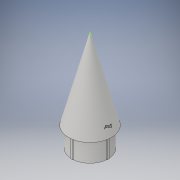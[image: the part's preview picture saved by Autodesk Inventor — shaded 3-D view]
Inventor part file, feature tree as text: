
AUTODESK INVENTOR PART (.ipt)
format: ipt  version: 2017 (Build 210142000, 142)  size: 165,376 bytes
history: native  units: in
note: dims shown in document units (in); Inventor stores cm internally (conversion verified against a paired STEP export)
features: revolve x4, sketch x2, extrude x1
ambient origin geometry x8: Origin, YZ Plane, XZ Plane, XY Plane, X Axis, Y Axis, Z Axis, Center Point
bodies: Solid1 (feature_tree)
feature tree (7):
  sketch  "Sketch1"  dims[d5=90.0deg d6=90.0deg]
  revolve  "Revolution1"  Angle=90.0deg
  revolve  "Revolution2"  [1 undecoded]
  extrude  "Extrusion1"  Depth=1.0in
  revolve  "Revolution3"  [1 undecoded]
  revolve  "Revolution4"  [1 undecoded]
  sketch  "Sketch2"  dims[d14=0.0625in d16=0.0625in d17=0.015in d18=0.0625in d19=0.0625in d21=0.0625in d22=0.0in d23=0.0625in d24=180.0deg d25=1.0in d26=0.0in d27=0.05in d28=90.0deg d29=90.0deg]
note: 3 required parameter values undecoded (feature->parameter linkage not recoverable at this tier; creation-order binding heuristic only, values carry confidence <= 0.55)
